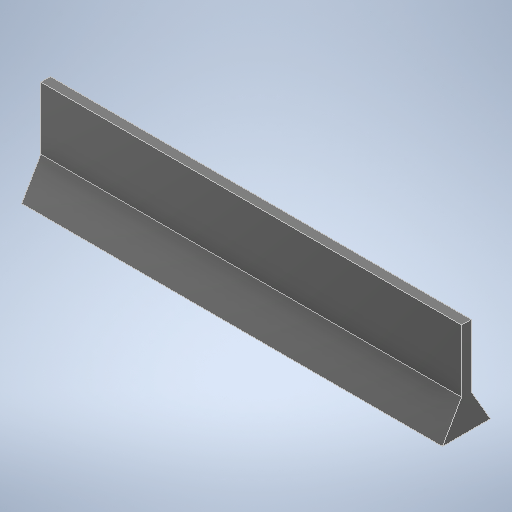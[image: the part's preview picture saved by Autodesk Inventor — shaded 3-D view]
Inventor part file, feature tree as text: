
AUTODESK INVENTOR PART (.ipt)
format: ipt  version: 2025.1 (Build 291241020, 241B)  size: 412,672 bytes
history: native  units: mm
features: sketch x3, extrude x2, projected_geometry x2, hole x1
ambient origin geometry x8: Origin, YZ Plane, XZ Plane, XY Plane, X Axis, Y Axis, Z Axis, Center Point
bodies: Solid1 (feature_tree)
feature tree (8):
  extrude  "Extrusion1"  Depth=50.0mm
  hole  "Hole1"  [1 undecoded]
  extrude  "Extrusion2"  Depth=5.0mm
  sketch  "Sketch1"  dims[d0=220.0mm d1=50.0mm]
  sketch  "Sketch2"  dims[d2=5.0mm d3=0.0mm d4=5.0mm]
  sketch  "Sketch3"  dims[d5=220.0mm d6=2.5mm d7=38.0mm d8=48.0mm d9=48.0mm d10=48.0mm d11=4.8mm d12=6.0mm d13=4.0mm d14=2.0mm d15=90.0deg d16=10.0mm d17=0.0mm d18=10.0mm d19=60.0deg d20=5.0mm d21=0.0mm d22=0.5mm d23=0.872665mm]
  projected_geometry  "Projected Loop1"
  projected_geometry  "Projected Loop2"
note: 1 required parameter value undecoded (feature->parameter linkage not recoverable at this tier; creation-order binding heuristic only, values carry confidence <= 0.55)
